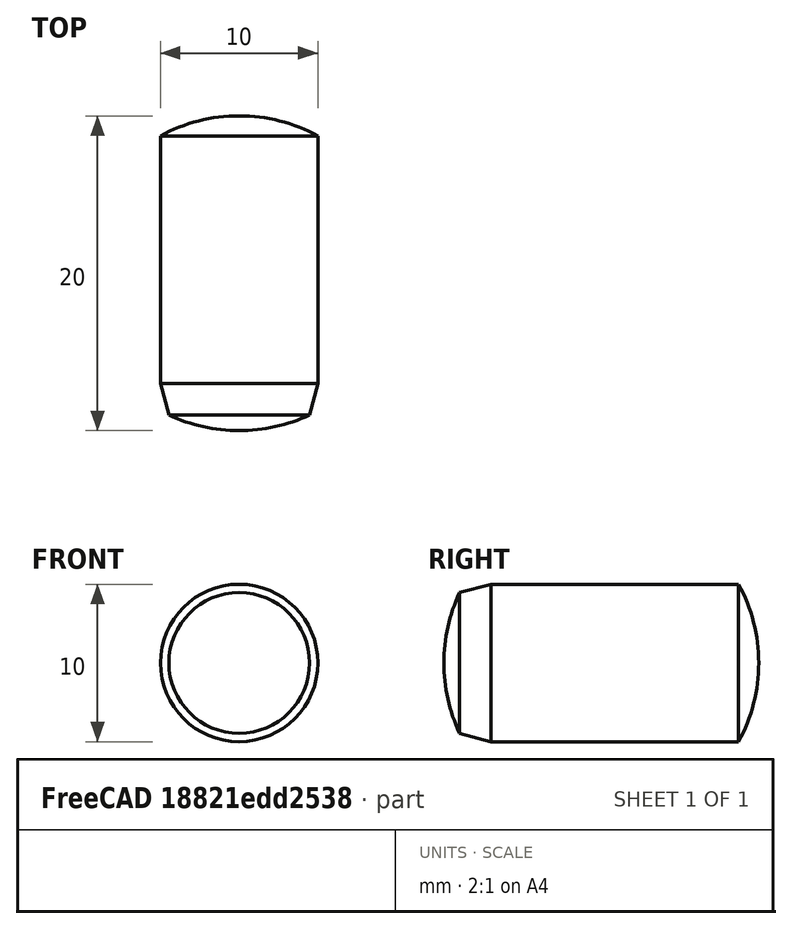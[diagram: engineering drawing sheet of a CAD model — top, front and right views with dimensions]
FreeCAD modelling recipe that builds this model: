
FCSTD DOCUMENT  (FreeCAD 0.15R4470 (Git))
Label: Zyl-Stift_DIN_6325-10x20
License: CC-BY 3.0
LicenseURL: http://creativecommons.org/licenses/by/3.0/
objects: Sketcher::SketchObject×1, PartDesign::Revolution×1
note: 3 computed .brp shape members not serialized (recipe doc carries the construction recipe); baked Part::Feature solids carry a one-line shape summary decoded from their .brp

FEATURE [Sketcher::SketchObject] Sketch
  Placement = pos=(0,0,0) rot=(0.57735,0.57735,0.57735;2.0944rad)
  sketch-geometry (5):
    g0: ArcOfCircle CenterX=9.4641 CenterY=0 CenterZ=0 NormalX=0 NormalY=0 NormalZ=1 Radius=10.4641 StartAngle=2.70085 EndAngle=3.14159
    g1: LineSegment StartX=-1.7e-11 StartY=4.4641 StartZ=0 EndX=2 EndY=5 EndZ=0
    g2: LineSegment StartX=2 StartY=5 StartZ=0 EndX=17.7281 EndY=5 EndZ=0
    g3: ArcOfCircle CenterX=8.5359 CenterY=0 CenterZ=0 NormalX=0 NormalY=0 NormalZ=1 Radius=10.4641 StartAngle=0 EndAngle=0.498176
    g4: LineSegment StartX=-1 StartY=0 StartZ=0 EndX=19 EndY=0 EndZ=0
  constraints (17):
    c: PointOnObject(g0,g-1)
    c: PointOnObject(g0,g-1)
    c: PointOnObject(g0,g-2)
    c: Coincident(g0,g1)
    c: Coincident(g1,g2)
    c: Horizontal(g2)
    c: PointOnObject(g3,g-1)
    c: Coincident(g3,g2)
    c: PointOnObject(g3,g-1)
    c: Coincident(g4,g0)
    c: Coincident(g4,g3)
    c: Equal(g0,g3)
    c: Angle(g4,g1) = 0.261799
    c: DistanceX(g4) = 20
    c: DistanceY(g-1,g1) = 5
    c: DistanceX(g1) = 2
    c: DistanceX(g0,g0) = 1
FEATURE [PartDesign::Revolution] Revolution  label="Zyl-Stift DIN 6325-10x20 #"
  Angle = 360
  Axis = (0,1,0)
  Base = (0,0,0)
  Placement = pos=(0,0,0) rot=(0.57735,0.57735,0.57735;2.0944rad)
  ReferenceAxis = -> Sketch [H_Axis]
  Sketch = -> Sketch
